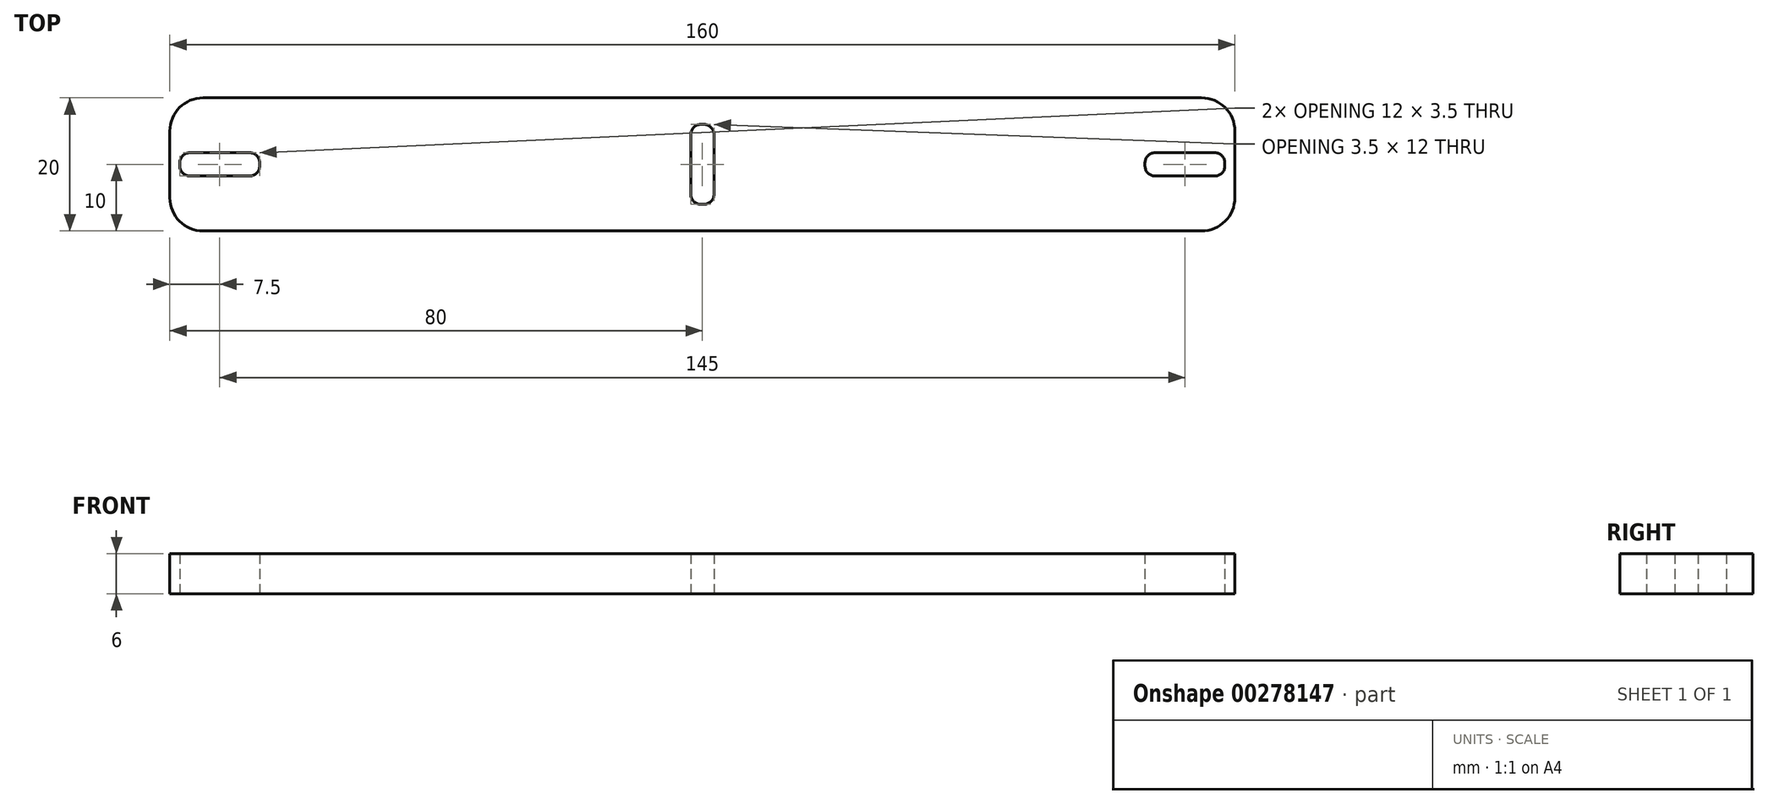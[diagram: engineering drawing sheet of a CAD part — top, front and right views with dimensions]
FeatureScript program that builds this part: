
annotation { "Feature Type Name" : "Feature", "Feature Type Description" : "" }
export const myFeature = defineFeature(function(context is Context, id is Id, definition is map)
    precondition{}
    {
        {
            var Q0;
            Q0=qCreatedBy(makeId("Top.planeOp"),FACE);
            var sketch = newSketch(context, id + "F0", { "sketchPlane" : qUnion([Q0])});
            skLineSegment(sketch, "E0.bottom", {"start": v(-72.5, 7.5) * mm, "end": v(72.5, 7.5) * mm, "construction": true});
            skLineSegment(sketch, "E0.top", {"start": v(-72.5, -7.5) * mm, "end": v(72.5, -7.5) * mm, "construction": true});
            skLineSegment(sketch, "E0.left", {"start": v(-72.5, 7.5) * mm, "end": v(-72.5, -7.5) * mm, "construction": true});
            skLineSegment(sketch, "E0.right", {"start": v(72.5, 7.5) * mm, "end": v(72.5, -7.5) * mm, "construction": true});
            skPoint(sketch, "E0.middle", {"position": v(0, 0) * mm});
            skLineSegment(sketch, "E1.bottom", {"start": v(-78.5, 1.75) * mm, "end": v(-66.5, 1.75) * mm});
            skLineSegment(sketch, "E1.top", {"start": v(-78.5, -1.75) * mm, "end": v(-66.5, -1.75) * mm});
            skLineSegment(sketch, "E1.left", {"start": v(-78.5, 1.75) * mm, "end": v(-78.5, -1.75) * mm});
            skLineSegment(sketch, "E1.right", {"start": v(-66.5, 1.75) * mm, "end": v(-66.5, -1.75) * mm});
            skPoint(sketch, "E1.middle", {"position": v(-72.5, 0) * mm});
            skLineSegment(sketch, "E2.bottom", {"start": v(66.5, 1.75) * mm, "end": v(78.5, 1.75) * mm});
            skLineSegment(sketch, "E2.top", {"start": v(66.5, -1.75) * mm, "end": v(78.5, -1.75) * mm});
            skLineSegment(sketch, "E2.left", {"start": v(66.5, 1.75) * mm, "end": v(66.5, -1.75) * mm});
            skLineSegment(sketch, "E2.right", {"start": v(78.5, 1.75) * mm, "end": v(78.5, -1.75) * mm});
            skPoint(sketch, "E2.middle", {"position": v(72.5, 0) * mm});
            skLineSegment(sketch, "E3.bottom", {"start": v(-1.75, 6) * mm, "end": v(1.75, 6) * mm});
            skLineSegment(sketch, "E3.top", {"start": v(-1.75, -6) * mm, "end": v(1.75, -6) * mm});
            skLineSegment(sketch, "E3.left", {"start": v(-1.75, 6) * mm, "end": v(-1.75, -6) * mm});
            skLineSegment(sketch, "E3.right", {"start": v(1.75, 6) * mm, "end": v(1.75, -6) * mm});
            skLineSegment(sketch, "E4.bottom", {"start": v(-80, 10) * mm, "end": v(80, 10) * mm});
            skLineSegment(sketch, "E4.top", {"start": v(-80, -10) * mm, "end": v(80, -10) * mm});
            skLineSegment(sketch, "E4.left", {"start": v(-80, 10) * mm, "end": v(-80, -10) * mm});
            skLineSegment(sketch, "E4.right", {"start": v(80, 10) * mm, "end": v(80, -10) * mm});
            skSolve(sketch);
        }
        {
            var Q0;
            Q0=makeQuery(id+"F0.imprint","IMPRINT",FACE,{"disambiguationData":[TD([[makeQuery(id+"F0.imprint","IMPRINT",EDGE,{"derivedFrom":sQuery(id+"F0.wireOp",EDGE,"E1.bottom")}),1.0]])]});
            extrude(context, id + "F1", {"entities" : qUnion([Q0]), "flatOperationType" : FlatOperationType.REMOVE, "offsetDistance" : 25 * mm, "depth" : 6 * mm, "domain" : OperationDomain.MODEL});
        }
        {
            var Q0;
            Q0=makeQuery(id+"F1.opExtrude","SWEPT_EDGE",EDGE,{"disambiguationData":[OSD([sQuery(id+"F0.wireOp",EDGE,"E1.bottom"),sQuery(id+"F0.wireOp",EDGE,"E1.left")])]});
            var Q1;
            Q1=makeQuery(id+"F1.opExtrude","SWEPT_EDGE",EDGE,{"disambiguationData":[OSD([sQuery(id+"F0.wireOp",EDGE,"E1.bottom"),sQuery(id+"F0.wireOp",EDGE,"E1.right")])]});
            var Q2;
            Q2=makeQuery(id+"F1.opExtrude","SWEPT_EDGE",EDGE,{"disambiguationData":[OSD([sQuery(id+"F0.wireOp",EDGE,"E1.top"),sQuery(id+"F0.wireOp",EDGE,"E1.right")])]});
            var Q3;
            Q3=makeQuery(id+"F1.opExtrude","SWEPT_EDGE",EDGE,{"disambiguationData":[OSD([sQuery(id+"F0.wireOp",EDGE,"E1.top"),sQuery(id+"F0.wireOp",EDGE,"E1.left")])]});
            var Q4;
            Q4=makeQuery(id+"F1.opExtrude","SWEPT_EDGE",EDGE,{"disambiguationData":[OSD([sQuery(id+"F0.wireOp",EDGE,"E3.bottom"),sQuery(id+"F0.wireOp",EDGE,"E3.left")])]});
            var Q5;
            Q5=makeQuery(id+"F1.opExtrude","SWEPT_EDGE",EDGE,{"disambiguationData":[OSD([sQuery(id+"F0.wireOp",EDGE,"E3.bottom"),sQuery(id+"F0.wireOp",EDGE,"E3.right")])]});
            var Q6;
            Q6=makeQuery(id+"F1.opExtrude","SWEPT_EDGE",EDGE,{"disambiguationData":[OSD([sQuery(id+"F0.wireOp",EDGE,"E3.top"),sQuery(id+"F0.wireOp",EDGE,"E3.right")])]});
            var Q7;
            Q7=makeQuery(id+"F1.opExtrude","SWEPT_EDGE",EDGE,{"disambiguationData":[OSD([sQuery(id+"F0.wireOp",EDGE,"E3.top"),sQuery(id+"F0.wireOp",EDGE,"E3.left")])]});
            var Q8;
            Q8=makeQuery(id+"F1.opExtrude","SWEPT_EDGE",EDGE,{"disambiguationData":[OSD([sQuery(id+"F0.wireOp",EDGE,"E2.bottom"),sQuery(id+"F0.wireOp",EDGE,"E2.right")])]});
            var Q9;
            Q9=makeQuery(id+"F1.opExtrude","SWEPT_EDGE",EDGE,{"disambiguationData":[OSD([sQuery(id+"F0.wireOp",EDGE,"E2.top"),sQuery(id+"F0.wireOp",EDGE,"E2.right")])]});
            var Q10;
            Q10=makeQuery(id+"F1.opExtrude","SWEPT_EDGE",EDGE,{"disambiguationData":[OSD([sQuery(id+"F0.wireOp",EDGE,"E2.bottom"),sQuery(id+"F0.wireOp",EDGE,"E2.left")])]});
            var Q11;
            Q11=makeQuery(id+"F1.opExtrude","SWEPT_EDGE",EDGE,{"disambiguationData":[OSD([sQuery(id+"F0.wireOp",EDGE,"E2.top"),sQuery(id+"F0.wireOp",EDGE,"E2.left")])]});
            fillet(context, id + "F2", {"entities" : qUnion([Q0, Q1, Q2, Q3, Q4, Q5, Q6, Q7, Q8, Q9, Q10, Q11]), "radius" : 1.5 * mm, "tangentPropagation" : true, "allowEdgeOverflow" : false});
        }
        {
            var Q0;
            Q0=makeQuery(id+"F1.opExtrude","SWEPT_EDGE",EDGE,{"disambiguationData":[OSD([sQuery(id+"F0.wireOp",EDGE,"E4.bottom"),sQuery(id+"F0.wireOp",EDGE,"E4.left")])]});
            var Q1;
            Q1=makeQuery(id+"F1.opExtrude","SWEPT_EDGE",EDGE,{"disambiguationData":[OSD([sQuery(id+"F0.wireOp",EDGE,"E4.top"),sQuery(id+"F0.wireOp",EDGE,"E4.left")])]});
            var Q2;
            Q2=makeQuery(id+"F1.opExtrude","SWEPT_EDGE",EDGE,{"disambiguationData":[OSD([sQuery(id+"F0.wireOp",EDGE,"E4.bottom"),sQuery(id+"F0.wireOp",EDGE,"E4.right")])]});
            var Q3;
            Q3=makeQuery(id+"F1.opExtrude","SWEPT_EDGE",EDGE,{"disambiguationData":[OSD([sQuery(id+"F0.wireOp",EDGE,"E4.top"),sQuery(id+"F0.wireOp",EDGE,"E4.right")])]});
            fillet(context, id + "F3", {"entities" : qUnion([Q0, Q1, Q2, Q3]), "radius" : 5 * mm, "tangentPropagation" : true, "allowEdgeOverflow" : false});
        }
    });
